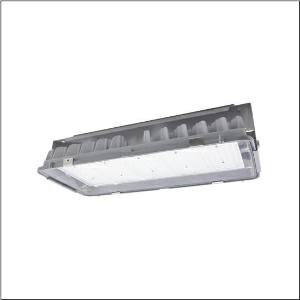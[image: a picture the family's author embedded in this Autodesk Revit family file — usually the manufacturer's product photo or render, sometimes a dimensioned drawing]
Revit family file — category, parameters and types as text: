
# Revit family: highbay_11xtreme_51hf61da4mma
name_source: partatom
category: Lighting Fixtures
units: mm (PartAtom-declared; Revit-internal decimal feet)

## family parameters
Cut with Voids When Loaded = No
Host = Face
Light Source = No
Part Type = Normal
Room Calculation Point = No
Round Connector Dimension = Use Diameter
Shared = No

## types (1)
- --- (1 x LED, 31500 lm, 170.8 W, 4000K)
    Apparent Load = 171 VA
    CIE Flux Codes = 88 96 99 100 100
    Color Rendering = 80
    Color Temperature = 4000K
    Default Elevation = 1800 mm
    Description = Highbay 11Xtreme, LED high bay luminaire, primary light control with lens, of PMMA, primary optical cover: cover, of toughened safety glass, light emission: direct distribution, primary light characteristic: symmetric, installation type: suspended mounting, surface-mounted, 1x LED module,for 1x LED, rated luminous flux: 31.500lm, luminous efficacy: 184lm/W, light colour: 840, colour temperature: 4000K, with cable H07RN-F 5x 1.5mm², mains connection: 220..240V, AC, 50/60Hz, cable length: 1,5m, rated input power: 171W, luminaire housing, of diecast aluminium, coated, silver, length: 595mm, width: 280mm, height: 195mm, protection rating (complete): IP66, insulation class (complete): insulation class I (protective earthing), certification: CE, ENEC, UKCA, protection symbol: D, ball protection: ball impact resistant according to DIN VDE 0710 part 13 (with chain suspension), impact resistance: IK08, permissible operating ambient temperature: -25..+60°C, reducing of maximum allowable ambient temperature of 5°C with ceiling mounting, packaging unit: 1 piece
    Height = 157 mm
    Lamp = 1 x LED
    Lamp Light Flux = 31500 lm
    Lamp Power = 170.8 W
    Lamp count = 1
    Length = 593 mm
    Luminous efficacy = 184 lm/W
    Manufacturer = Siteco
    ModVariant = No
    Model = 51HF61DA4MMA
    Mounting Place = Ceiling
    Mounting Type = Pendant
    Number of Poles = 1
    OnlyDefault = Yes
    Power Factor = 1
    Product Name = Highbay 11Xtreme
    Product group = LED high bay luminaire
    ProductGroupID = 903
    Protection Class = Protection class I
    Protection Degree = IP 66
    RLX_Detail_Level = 1
    RLX_Emergency_Light_Flux = 0 lm
    RLX_Emergency_Type = 0
    RLX_Emergency_Type_DB = No
    RlxData = <blob elided: 27885 chars, md5=4a2d395c>
    Socket = socket
    Standby Power = 0 W
    System Light Flux = 31501 lm
    System Power = 171 W
    Type Comments = factory setting: luminous flux: 100 % | dim-lin: 254 | 1132 mA
    Type Image = l_1258342.jpg
    URL = http://relux.com
    VarID = @adj_035755
    Voltage = 0 V
    Weight = 0.00 kg
    Width = 278 mm

## geometry (parser evidence)
native form markers: Blend x4, Sweep x13
no freeform markers — native parametric forms only
